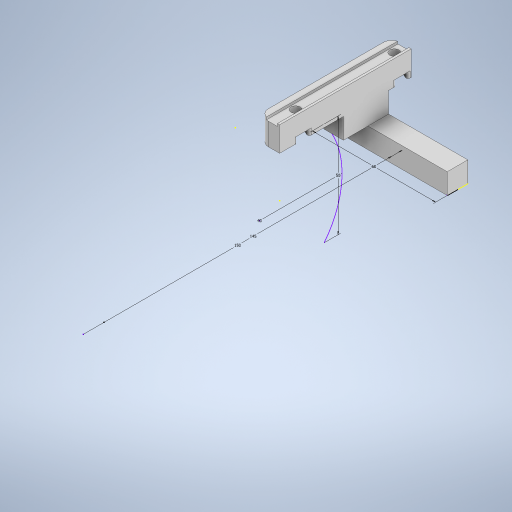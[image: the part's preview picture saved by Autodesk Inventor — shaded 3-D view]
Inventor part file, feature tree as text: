
AUTODESK INVENTOR PART (.ipt)
format: ipt  version: 2024 (Build 280153000, 153)  size: 349,184 bytes
history: native  units: in
note: dims shown in document units (in); Inventor stores cm internally (conversion verified against a paired STEP export)
features: sketch x9, extrude x5, projected_geometry x4, fillet x2
ambient origin geometry x8: Origin, YZ Plane, XZ Plane, XY Plane, X Axis, Y Axis, Z Axis, Center Point
bodies: Solid1 (feature_tree)
feature tree (20):
  extrude  "Extrusion1"  Depth=2.5197in
  extrude  "Extrusion2"  Depth=1.8898in
  extrude  "Extrusion3"  Depth=0.4724in TaperAngle=0.0deg
  fillet  "Fillet1"  Radius=0.0433in
  fillet  "Fillet2"  Radius=0.2126in
  extrude  "Extrusion19"  Depth=0.4724in TaperAngle=0.0deg
  extrude  "Extrusion20"  Depth=0.1181in TaperAngle=0.0deg
  sketch  "Sketch32"  dims[d17=0.1772in]
  sketch  "Sketch34"  dims[d18=0.0394in]
  sketch  "Sketch36"  dims[d19=0.1575in]
  sketch  "Sketch37"  dims[d76=0.4724in d107=0.102in d108=0.8661in d109=0.3937in d110=0.0in d111=1.8898in d112=0.3937in d113=2.3622in d114=0.3937in d115=0.3937in d116=0.0in d121=2.3622in d122=5.9055in d123=5.7087in d126=1.9685in d127=1.5748in d42=0.0197in d43=0.0344in d44=0.0197in d45=0.0344in d46=0.0in d47=0.0in d48=0.0in d49=0.0in d50=0.0in d51=0.0in d52=0.0in d53=0.0in d55=0.0197in d56=0.0344in d57=0.0197in d58=0.0344in d60=0.0197in d61=0.0344in d62=0.0197in d63=0.0344in d72=0.0197in d73=0.0344in d74=0.0197in d75=0.0344in]
  sketch  "Sketch1"  dims[d1=0.374in d2=2.5197in]
  sketch  "Sketch2"  dims[d3=0.1772in d4=1.8898in]
  sketch  "Sketch3"  dims[d6=0.1457in d7=0.4724in d8=0.0in d9=0.0433in d10=0.2126in]
  projected_geometry  "Projected Loop2"
  projected_geometry  "Projected Loop3"
  projected_geometry  "Projected Loop4"
  projected_geometry  "Projected Loop5"
  sketch  "Sketch28"  dims[d11=0.0472in d12=0.4724in d13=0.0in]
  sketch  "Sketch29"  dims[d14=0.2953in d15=0.1181in d16=0.0in]
